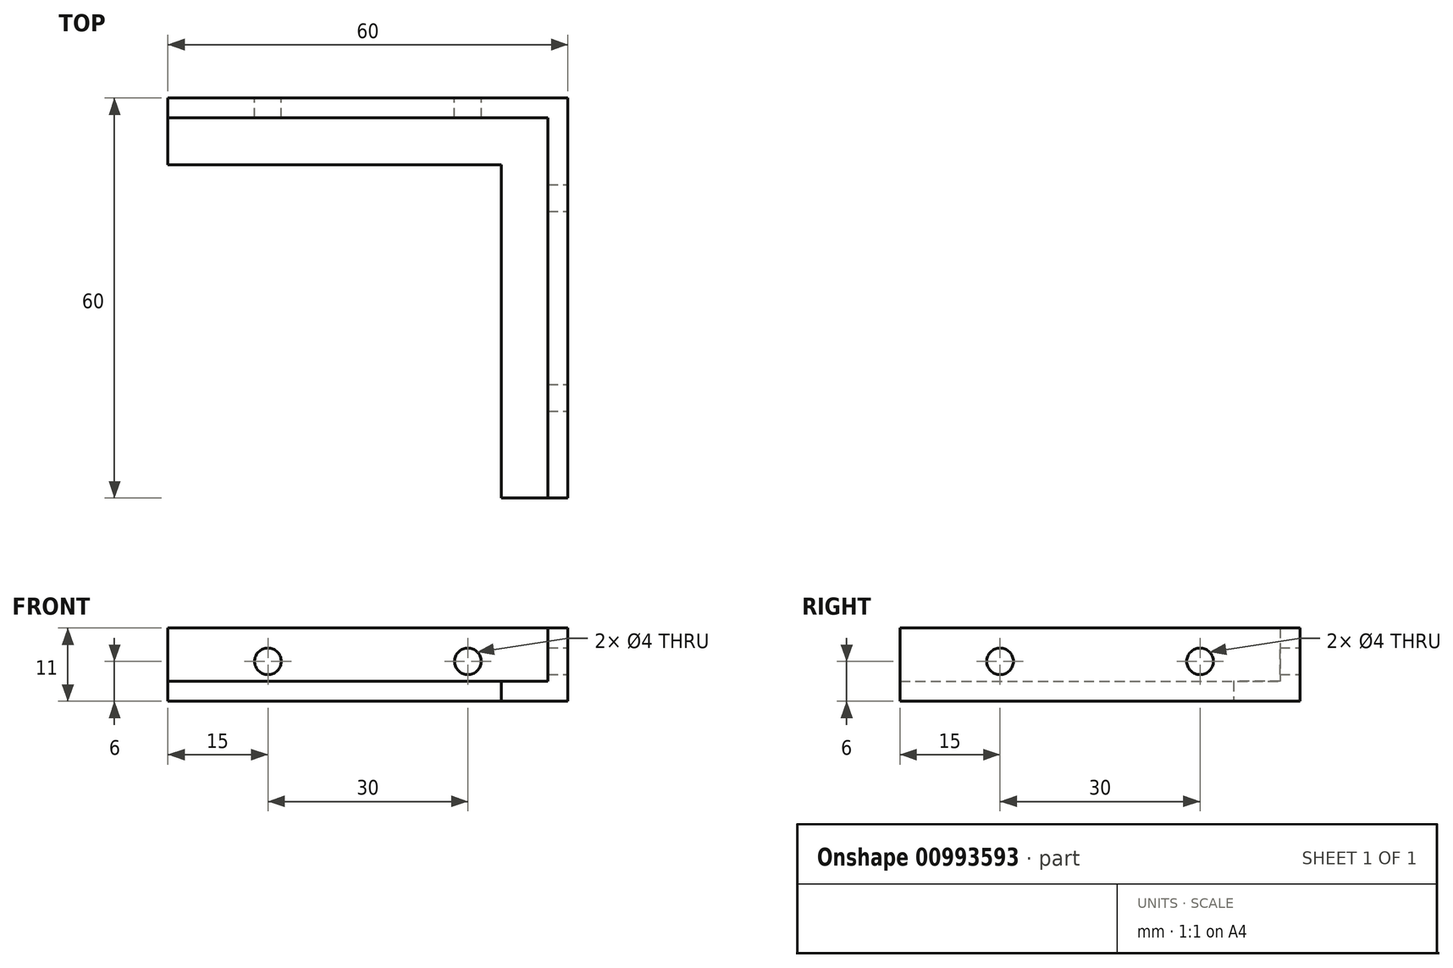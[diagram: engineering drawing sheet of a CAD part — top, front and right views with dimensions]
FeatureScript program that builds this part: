
annotation { "Feature Type Name" : "Feature", "Feature Type Description" : "" }
export const myFeature = defineFeature(function(context is Context, id is Id, definition is map)
    precondition{}
    {
        {
            var Q0;
            Q0=qCreatedBy(makeId("Top.planeOp"),FACE);
            var sketch = newSketch(context, id + "F0", { "sketchPlane" : qUnion([Q0])});
            skLineSegment(sketch, "E0.bottom", {"start": v(-60, 0) * mm, "end": v(0, 0) * mm});
            skLineSegment(sketch, "E0.top", {"start": v(-60, -10) * mm, "end": v(-10, -10) * mm});
            skLineSegment(sketch, "E0.left", {"start": v(-60, 0) * mm, "end": v(-60, -10) * mm});
            skLineSegment(sketch, "E1", {"start": v(0, -60) * mm, "end": v(-10, -60) * mm});
            skLineSegment(sketch, "E2", {"start": v(-10, -60) * mm, "end": v(-10, -10) * mm});
            skLineSegment(sketch, "E3", {"start": v(0, 0) * mm, "end": v(0, -60) * mm});
            skSolve(sketch);
        }
        {
            var Q0;
            Q0 = qSketchRegion(id + "F0", true);
            extrude(context, id + "F1", {"entities" : qUnion([Q0]), "depth" : 3 * mm, "offsetDistance" : 25 * mm});
        }
        {
            var Q0;
            Q0=makeQuery(id+"F1.opExtrude","CAP_FACE",FACE,{"disambiguationData":[OSD([sQuery(id+"F0.wireOp",EDGE,"E0.bottom"),sQuery(id+"F0.wireOp",EDGE,"E0.top"),sQuery(id+"F0.wireOp",EDGE,"E0.left"),sQuery(id+"F0.wireOp",EDGE,"E1"),sQuery(id+"F0.wireOp",EDGE,"E2"),sQuery(id+"F0.wireOp",EDGE,"E3")])],"isStart":false});
            var sketch = newSketch(context, id + "F2", { "sketchPlane" : qUnion([Q0])});
            skLineSegment(sketch, "E4", {"start": v(-60, 0) * mm, "end": v(0, 0) * mm});
            skLineSegment(sketch, "E5", {"start": v(0, 0) * mm, "end": v(0, -60) * mm});
            skLineSegment(sketch, "E6", {"start": v(0, -60) * mm, "end": v(-3, -60) * mm});
            skLineSegment(sketch, "E7", {"start": v(-3, -60) * mm, "end": v(-3, -3) * mm});
            skLineSegment(sketch, "E8", {"start": v(-3, -3) * mm, "end": v(-60, -3) * mm});
            skLineSegment(sketch, "E9", {"start": v(-60, -3) * mm, "end": v(-60, 0) * mm});
            skSolve(sketch);
        }
        {
            var Q0;
            Q0 = qSketchRegion(id + "F2", true);
            extrude(context, id + "F3", {"entities" : qUnion([Q0]), "operationType" : NewBodyOperationType.ADD, "depth" : 8 * mm, "offsetDistance" : 25 * mm});
        }
        {
            var Q0;
            Q0=makeQuery(id+"F3.boolean.opBoolean","MERGE",FACE,{"derivedFrom":[makeQuery(id+"F1.opExtrude","SWEPT_FACE",FACE,{"disambiguationData":[OSD([sQuery(id+"F0.wireOp",EDGE,"E3")])]}),makeQuery(id+"F3.opExtrude","SWEPT_FACE",FACE,{"disambiguationData":[OSD([sQuery(id+"F2.wireOp",EDGE,"E5")])]})]});
            var sketch = newSketch(context, id + "F4", { "sketchPlane" : qUnion([Q0])});
            skCircle(sketch, "E10", {"center": v(-15, 6) * mm, "radius": 2 * mm});
            skCircle(sketch, "E11", {"center": v(-45, 6) * mm, "radius": 2 * mm});
            skSolve(sketch);
        }
        {
            var Q0;
            Q0 = qSketchRegion(id + "F4", true);
            extrude(context, id + "F5", {"entities" : qUnion([Q0]), "operationType" : NewBodyOperationType.REMOVE, "oppositeDirection" : true, "depth" : 4 * mm, "offsetDistance" : 25 * mm});
        }
        {
            var Q0;
            Q0=makeQuery(id+"F3.boolean.opBoolean","MERGE",FACE,{"derivedFrom":[makeQuery(id+"F1.opExtrude","SWEPT_FACE",FACE,{"disambiguationData":[OSD([sQuery(id+"F0.wireOp",EDGE,"E0.bottom")])]}),makeQuery(id+"F3.opExtrude","SWEPT_FACE",FACE,{"disambiguationData":[OSD([sQuery(id+"F2.wireOp",EDGE,"E4")])]})]});
            var sketch = newSketch(context, id + "F6", { "sketchPlane" : qUnion([Q0])});
            skCircle(sketch, "E12", {"center": v(45, 6) * mm, "radius": 2 * mm});
            skCircle(sketch, "E13", {"center": v(15, 6) * mm, "radius": 2 * mm});
            skSolve(sketch);
        }
        {
            var Q0;
            Q0 = qSketchRegion(id + "F6", true);
            extrude(context, id + "F7", {"entities" : qUnion([Q0]), "operationType" : NewBodyOperationType.REMOVE, "oppositeDirection" : true, "depth" : 6 * mm, "offsetDistance" : 25 * mm});
        }
    });
